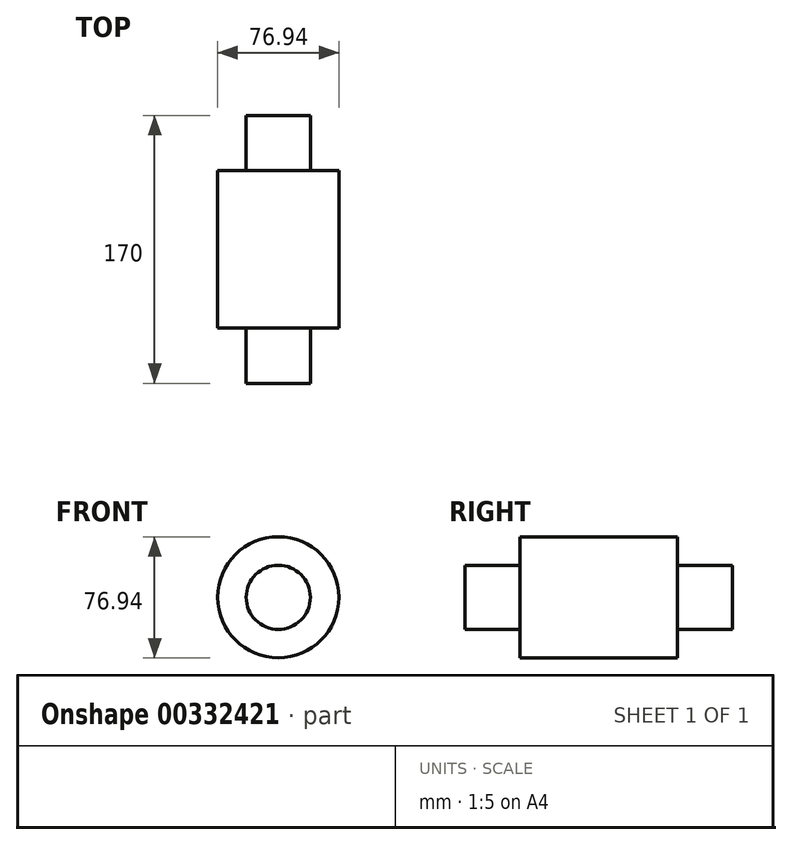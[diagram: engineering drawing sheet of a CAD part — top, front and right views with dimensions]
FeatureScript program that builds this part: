
annotation { "Feature Type Name" : "Feature", "Feature Type Description" : "" }
export const myFeature = defineFeature(function(context is Context, id is Id, definition is map)
    precondition{}
    {
        {
            var Q0;
            Q0=qCreatedBy(makeId("Front.planeOp"),FACE);
            var sketch = newSketch(context, id + "F0", { "sketchPlane" : qUnion([Q0])});
            skCircle(sketch, "E0", {"center": v(0, 0) * mm, "radius": 20.37 * mm});
            skCircle(sketch, "E1", {"center": v(0, 0) * mm, "radius": 38.47 * mm});
            skSolve(sketch);
        }
        {
            var Q0;
            Q0=makeQuery(id+"F0.imprint","IMPRINT",FACE,{"disambiguationData":[TD([[makeQuery(id+"F0.imprint","IMPRINT",EDGE,{"derivedFrom":sQuery(id+"F0.wireOp",EDGE,"E0")}),-1.0]])]});
            extrude(context, id + "F1", {"entities" : qUnion([Q0]), "depth" : 50 * mm, "offsetDistance" : 25 * mm});
        }
        {
            var Q0;
            Q0=makeQuery(id+"F0.imprint","IMPRINT",FACE,{"disambiguationData":[TD([[makeQuery(id+"F0.imprint","IMPRINT",EDGE,{"derivedFrom":sQuery(id+"F0.wireOp",EDGE,"E0")}),1.0]])]});
            extrude(context, id + "F2", {"entities" : qUnion([Q0]), "operationType" : NewBodyOperationType.ADD, "depth" : 85 * mm, "offsetDistance" : 25 * mm});
        }
        {
            var Q0;
            Q0=makeQuery(id+"F0.imprint","IMPRINT",FACE,{"disambiguationData":[TD([[makeQuery(id+"F0.imprint","IMPRINT",EDGE,{"derivedFrom":sQuery(id+"F0.wireOp",EDGE,"E0")}),1.0]])]});
            extrude(context, id + "F3", {"entities" : qUnion([Q0]), "operationType" : NewBodyOperationType.ADD, "oppositeDirection" : true, "depth" : 85 * mm, "offsetDistance" : 25 * mm});
        }
        {
            var Q0;
            Q0=makeQuery(id+"F0.imprint","IMPRINT",FACE,{"disambiguationData":[TD([[makeQuery(id+"F0.imprint","IMPRINT",EDGE,{"derivedFrom":sQuery(id+"F0.wireOp",EDGE,"E0")}),-1.0]])]});
            extrude(context, id + "F4", {"entities" : qUnion([Q0]), "operationType" : NewBodyOperationType.ADD, "oppositeDirection" : true, "depth" : 50 * mm, "offsetDistance" : 25 * mm});
        }
    });
